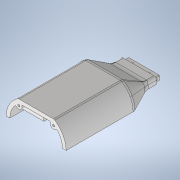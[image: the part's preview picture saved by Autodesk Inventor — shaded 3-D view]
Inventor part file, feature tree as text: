
AUTODESK INVENTOR PART (.ipt)
format: ipt  version: 2021 (Build 250183000, 183)  size: 1,669,120 bytes
history: native  units: mm
features: fillet x20, extrude x17, sketch x17, other x8, plane x4, mirror x4, delete_face x2, hole x2, loft x1
ambient origin geometry x8: Origin, YZ Plane, XZ Plane, XY Plane, X Axis, Y Axis, Z Axis, Center Point
bodies: Volumenkörper8 (feature_tree), Volumenkörper15 (feature_tree), Volumenkörper16 (feature_tree), Volumenkörper17 (feature_tree)
feature tree (75):
  extrude  "Extrusion2"  Depth=7.0mm
  extrude  "Extrusion3"  Depth=68.0mm
  fillet  "Rundung4"  Radius=12.0mm
  plane  "Arbeitsebene3"
  fillet  "Rundung5"  Radius=34.0mm
  plane  "Arbeitsebene4"
  extrude  "Extrusion4"  Depth=30.0mm TaperAngle=0.0deg
  loft  "Erhebung5"
  plane  "Arbeitsebene5"
  extrude  "Extrusion7"  Depth=10.0mm TaperAngle=0.0deg
  mirror  "Spiegeln1"
  extrude  "Extrusion9"  Depth=60.0mm
  delete_face  "Fläche löschen3"
  extrude  "Extrusion18"  Depth=57.0mm
  extrude  "Extrusion11"  Depth=50.0mm TaperAngle=0.0deg
  mirror  "Spiegeln5"
  mirror  "Spiegeln6"
  fillet  "Rundung11"  [1 undecoded]
  sketch  "Skizze18"  dims[d42=4.0mm d43=4.0mm]
  extrude  "Extrusion19"  Depth=13.0mm
  fillet  "Rundung21"  Radius=43.0mm
  extrude  "Extrusion14"  Depth=125.0mm
  mirror  "Spiegeln3"
  delete_face  "Fläche löschen4"
  hole  "Bohrung3"  [1 undecoded]
  hole  "Bohrung4"  [1 undecoded]
  extrude  "Extrusion20"  Depth=10.0mm
  fillet  "Rundung22"  Radius=123.25mm
  other  "Kombinieren12"
  other  "Kombinieren13"
  other  "Kombinieren14"
  other  "Kombinieren15"
  fillet  "Rundung23"  Radius=121.25mm
  fillet  "Rundung24"  Radius=2.0mm
  fillet  "Rundung25"  Radius=19.0mm
  fillet  "Rundung26"  Radius=12.75mm
  fillet  "Rundung27"  Radius=65.0mm
  fillet  "Rundung28"  Radius=13.0mm
  fillet  "Rundung29"  Radius=43.0mm
  fillet  "Rundung30"  Radius=168.5mm
  fillet  "Rundung31"  [1 undecoded]
  extrude  "Extrusion21"  TaperAngle=0.0deg  [1 undecoded]
  extrude  "Extrusion22"  TaperAngle=0.0deg  [1 undecoded]
  extrude  "Extrusion23"  TaperAngle=0.0deg  [1 undecoded]
  fillet  "Rundung32"  [1 undecoded]
  fillet  "Rundung33"  [1 undecoded]
  fillet  "Rundung34"  Radius=101.5mm
  extrude  "Extrusion24"  Depth=0.5mm
  extrude  "Extrusion25"  Depth=0.5mm
  fillet  "Rundung35"  Radius=10.0mm
  other  "Kombinieren16"
  extrude  "Extrusion26"  Depth=0.5mm
  extrude  "Extrusion28"  Depth=0.5mm
  fillet  "Rundung36"  Radius=25.0mm
  other  "Kombinieren17"
  fillet  "Rundung37"  Radius=50.0mm
  sketch  "Skizze10"  dims[d33=7.0mm d34=7.0mm]
  sketch  "Skizze11"  dims[d35=7.0mm d36=68.0mm d37=12.0mm d38=34.0mm]
  sketch  "Skizze16"  dims[d39=0.0mm d40=30.0mm d41=0.0mm]
  plane  "Arbeitsebene6"
  sketch  "Skizze24"  dims[d44=4.0mm d45=10.0mm d46=0.0mm]
  sketch  "Skizze26"  dims[d49=1.0mm d50=60.0mm d62=5.0mm]
  sketch  "Skizze29"  dims[d70=35.0mm d72=7.0mm d82=75.0mm d84=57.0mm d85=7.0mm]
  sketch  "Skizze32"  dims[d87=50.0mm d88=130.0mm d89=0.0mm d92=0.0mm d93=90.0deg]
  other  "Kanten7"
  other  "Kanten8"
  sketch  "Skizze36"  dims[d128=80.0mm d129=13.0mm d130=43.0mm]
  sketch  "Skizze37"  dims[d133=12.15mm d134=125.0mm]
  sketch  "Skizze39"  dims[d135=10.0mm d137=125.0mm d138=0.0mm]
  sketch  "Skizze40"  dims[d150=10.0mm d151=146.75mm]
  sketch  "Skizze41"  dims[d152=10.0mm d153=91.5mm d154=10.0mm d155=123.25mm d156=121.25mm d157=0.0mm d168=2.0mm]
  sketch  "Skizze42"  dims[d169=18.0mm d170=10.0mm d171=0.0mm d172=19.0mm d174=12.75mm d175=0.0mm d189=65.0mm d190=0.0mm d191=13.0mm d192=43.0mm d193=168.5mm]
  sketch  "Skizze43"  dims[d194=4.2mm d195=6.0mm d196=4.0mm d197=2.0mm d198=90.0deg d199=25.0mm d200=0.0mm d201=0.0mm]
  sketch  "Skizze44"  dims[d202=0.0mm d203=0.0mm]
  sketch  "Skizze47"  dims[d204=0.0mm d205=0.0mm d206=0.0mm d207=0.0mm d208=0.0mm d212=101.5mm d218=22.0mm d219=22.0mm d220=10.0mm d221=180.25mm d223=25.0mm d224=25.0mm d225=50.0mm d226=91.5mm d227=91.5mm d228=10.0mm d248=1.7mm d249=6.0mm d250=4.0mm d251=2.0mm d252=90.0deg d253=8.5mm d254=0.0mm d255=182.4mm d265=33.0mm d267=7.0mm d270=7.0mm d271=7.0mm d287=0.0mm d288=90.0deg d289=50.0mm d290=50.0mm d291=24.5mm d292=10.0mm d293=0.0mm d294=16.75mm d295=0.0mm d296=16.000054mm d297=19.0mm d298=20.0mm d299=10.0mm d300=19.0mm d301=10.000054mm d302=54.75mm d303=0.0mm d304=2.0mm d308=10.0mm d310=19.0mm d314=14.75mm d315=0.0mm d316=2.0mm d317=10.0mm d318=10.0mm d319=5.0mm d320=10.0mm d321=3.0mm d322=2.0mm d323=1.5mm d324=20.0mm d325=2.0mm d326=2.4mm d328=5.0mm d329=10.0mm d330=0.0mm d331=2.4mm d332=3.5mm d333=5.0mm d334=69.25mm d335=0.0mm d336=16.2mm d337=12.0mm d338=32.9mm d339=29.0mm d340=20.0mm d341=0.0mm d342=2.0mm d343=2.0mm d344=1.5mm d345=4.2mm d346=4.2mm d347=15.0mm d348=0.0mm d349=7.9mm d351=7.9mm d352=27.8mm d353=148.9mm d354=127.15mm d355=31.5mm d356=18.7mm d357=27.8mm d358=27.8mm d359=148.9mm d360=127.15mm d361=27.8mm d362=27.8mm d363=18.7mm d364=31.5mm d365=18.7mm d366=31.5mm d367=31.5mm d368=18.7mm d369=40.0mm d370=30.65mm d371=0.0mm d372=2.0mm d373=22.0mm d374=11.0mm d375=0.0mm d376=10.900173mm d377=37.25mm d378=0.0mm d379=22.4mm d387=25.0mm d388=10.0mm d390=29.0mm d391=25.0mm d392=15.0mm d393=0.0mm d394=2.0mm d395=1.5mm d396=40.0mm d327=1.0mm d380=0.5mm d381=0.872665mm d382=0.5mm d383=0.872665mm]
note: 9 required parameter values undecoded (feature->parameter linkage not recoverable at this tier; creation-order binding heuristic only, values carry confidence <= 0.55)
